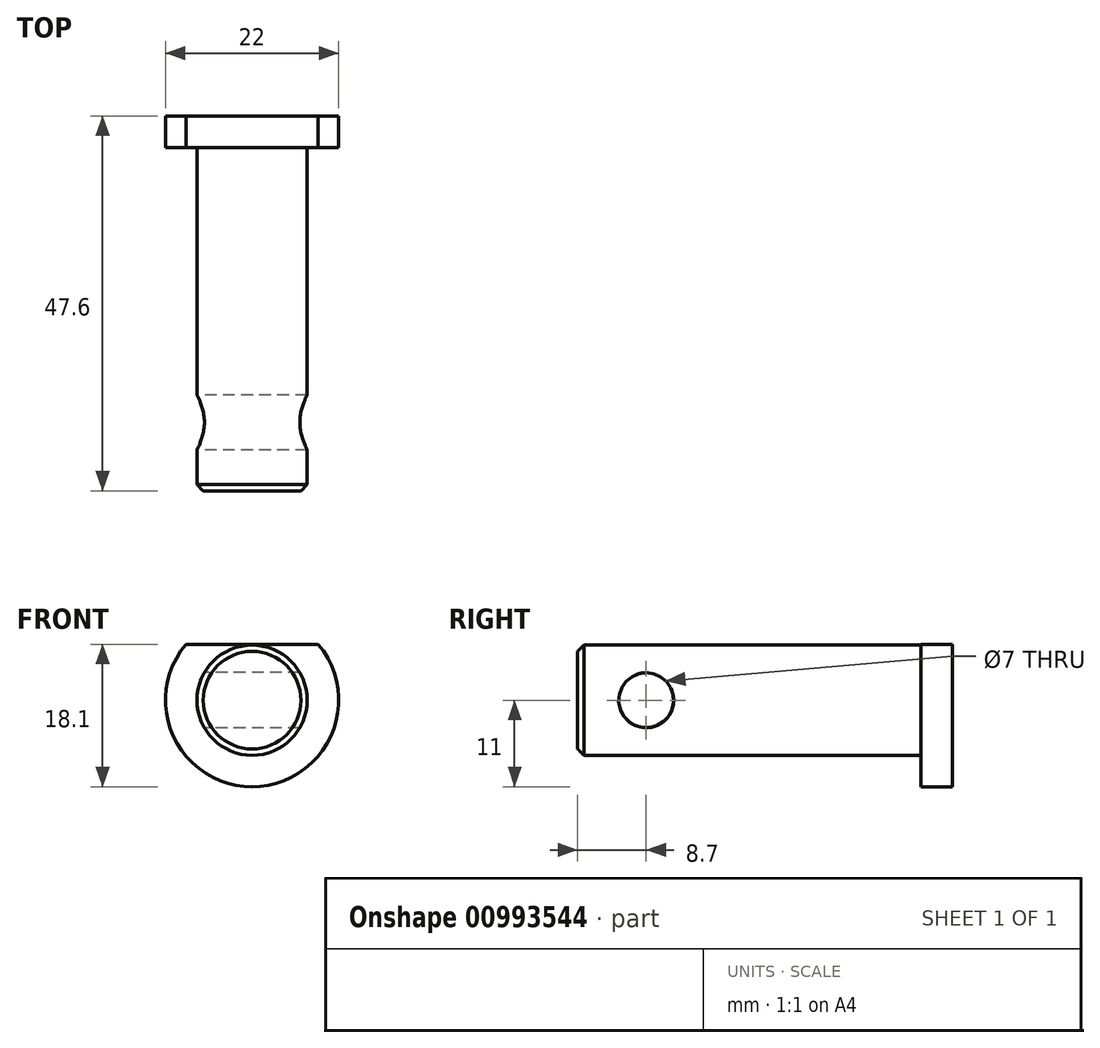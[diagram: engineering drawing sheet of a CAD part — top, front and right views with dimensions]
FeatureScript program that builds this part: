
annotation { "Feature Type Name" : "Feature", "Feature Type Description" : "" }
export const myFeature = defineFeature(function(context is Context, id is Id, definition is map)
    precondition{}
    {
        {
            var Q0;
            Q0=qCreatedBy(makeId("Front.planeOp"),FACE);
            var sketch = newSketch(context, id + "F0", { "sketchPlane" : qUnion([Q0])});
            skCircle(sketch, "E0", {"center": v(0, 0) * mm, "radius": 11 * mm});
            skCircle(sketch, "E1", {"center": v(0, 0) * mm, "radius": 7 * mm});
            skLineSegment(sketch, "E2", {"start": v(-8.4, 7.1) * mm, "end": v(8.4, 7.1) * mm});
            skSolve(sketch);
        }
        {
            var Q0;
            {var subQ4=sQuery(id+"F0.wireOp",EDGE,"E1");Q0=makeQuery(id+"F0.imprint","IMPRINT",FACE,{"disambiguationData":[TD([[makeQuery(id+"F0.imprint","IMPRINT",EDGE,{"derivedFrom":subQ4}),-1.0]])]});}
            extrude(context, id + "F1", {"entities" : qUnion([Q0]), "depth" : 4 * mm, "offsetDistance" : 25.4 * mm});
        }
        {
            var Q0;
            Q0=makeQuery(id+"F0.imprint","IMPRINT",FACE,{"disambiguationData":[TD([[makeQuery(id+"F0.imprint","IMPRINT",EDGE,{"derivedFrom":sQuery(id+"F0.wireOp",EDGE,"E1")}),1.0]])]});
            extrude(context, id + "F2", {"entities" : qUnion([Q0]), "operationType" : NewBodyOperationType.ADD, "depth" : 47.6 * mm, "offsetDistance" : 25.4 * mm});
        }
        {
            var Q0;
            Q0=makeQuery(id+"F2.opExtrude","CAP_EDGE",EDGE,{"disambiguationData":[OSD([sQuery(id+"F0.wireOp",EDGE,"E1")])],"isStart":false});
            chamfer(context, id + "F3", {"entities" : qUnion([Q0]), "width" : .8 * mm, "tangentPropagation" : true});
        }
        {
            var Q0;
            Q0=qCreatedBy(makeId("Right.planeOp"),FACE);
            var sketch = newSketch(context, id + "F4", { "sketchPlane" : qUnion([Q0])});
            skCircle(sketch, "E3", {"center": v(-38.9, 0) * mm, "radius": 3.5 * mm});
            skSolve(sketch);
        }
        {
            var Q0;
            Q0 = qSketchRegion(id + "F4", true);
            extrude(context, id + "F5", {"entities" : qUnion([Q0]), "operationType" : NewBodyOperationType.REMOVE, "depth" : 14.3 * mm, "offsetDistance" : 25.4 * mm, "hasSecondDirection" : true, "secondDirectionOppositeDirection" : true, "secondDirectionDepth" : 14.4 * mm});
        }
    });
